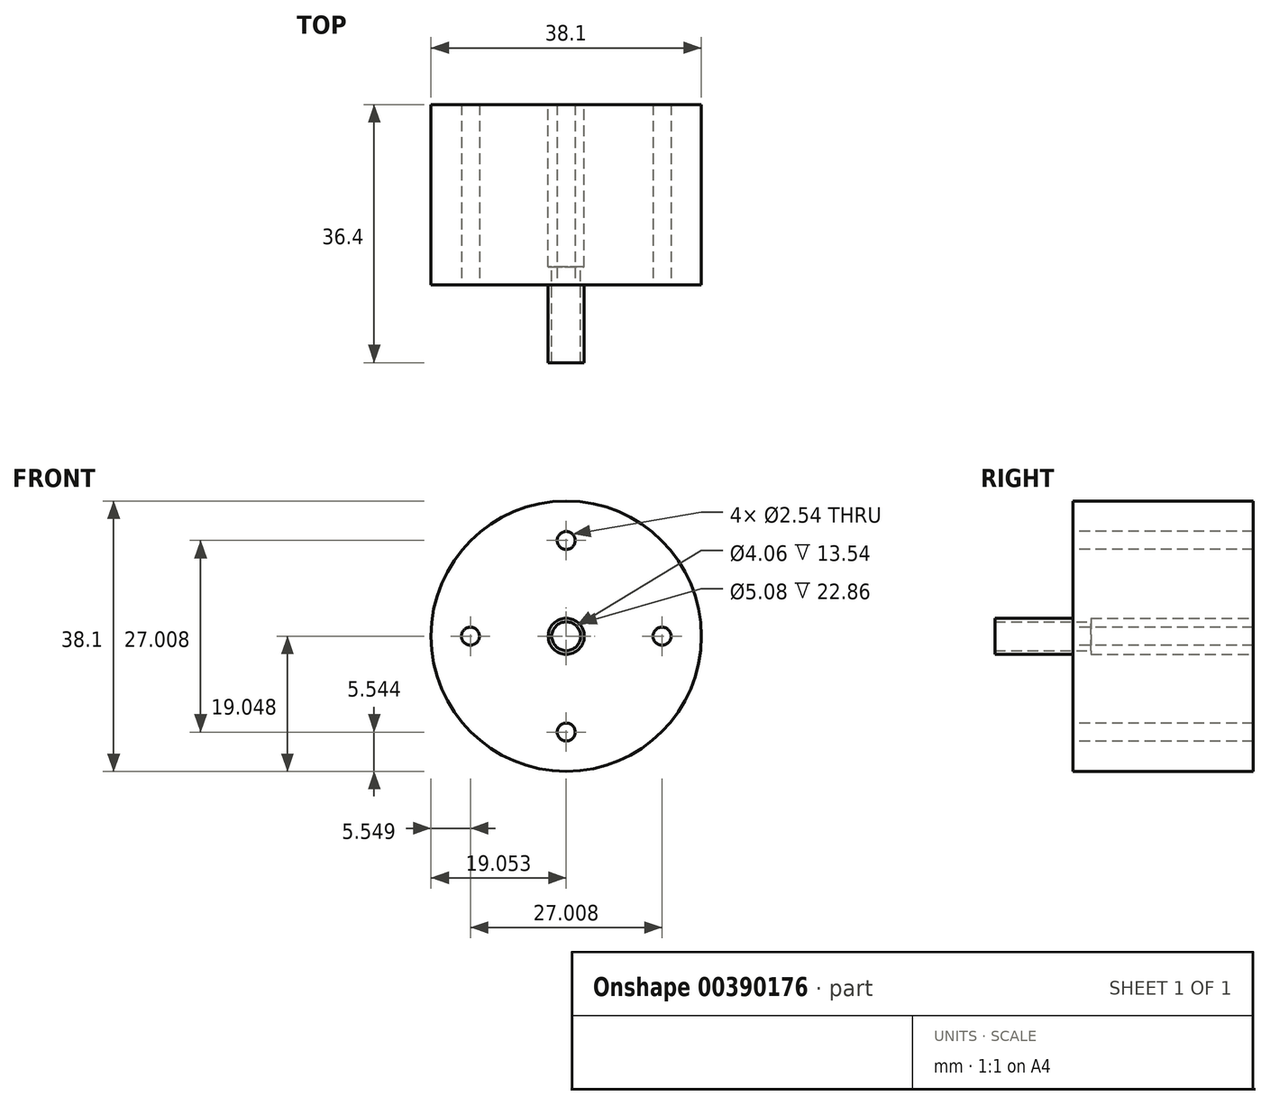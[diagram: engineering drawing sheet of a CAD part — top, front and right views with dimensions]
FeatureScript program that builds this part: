
annotation { "Feature Type Name" : "Feature", "Feature Type Description" : "" }
export const myFeature = defineFeature(function(context is Context, id is Id, definition is map)
    precondition{}
    {
        {
            var Q0;
            Q0=qCreatedBy(makeId("Front.planeOp"),FACE);
            var sketch = newSketch(context, id + "F0", { "sketchPlane" : qUnion([Q0])});
            skCircle(sketch, "E0", {"center": v(-6.44, 11.52) * mm, "radius": 19.05 * mm});
            skSolve(sketch);
        }
        {
            var Q0;
            Q0=qSketchRegion(id+"F0",true);
            extrude(context, id + "F1", {"entities" : qUnion([Q0]), "depth" : 25.4 * mm});
        }
        {
            var Q0;
            Q0=makeQuery(id+"F1.opExtrude","CAP_FACE",FACE,{"disambiguationData":[OSD([sQuery(id+"F0.wireOp",EDGE,"E0")])],"isStart":false});
            var sketch = newSketch(context, id + "F2", { "sketchPlane" : qUnion([Q0])});
            skCircle(sketch, "E1", {"center": v(-6.44, 11.52) * mm, "radius": 2.54 * mm});
            skCircle(sketch, "E2", {"center": v(-6.44, 11.52) * mm, "radius": 2.03 * mm});
            skSolve(sketch);
        }
        {
            var Q0;
            Q0=qSketchRegion(id+"F2",true);
            extrude(context, id + "F3", {"entities" : qUnion([Q0]), "operationType" : NewBodyOperationType.ADD, "depth" : 11 * mm});
        }
        {
            var Q0;
            Q0=makeQuery(id+"F3.boolean.opBoolean","SPLIT",FACE,{"disambiguationData":[TD([makeQuery(id+"F3.opExtrude","SWEPT_FACE",FACE,{"disambiguationData":[OSD([sQuery(id+"F2.wireOp",EDGE,"E2")])]})])],"derivedFrom":makeQuery(id+"F1.opExtrude","CAP_FACE",FACE,{"disambiguationData":[OSD([sQuery(id+"F0.wireOp",EDGE,"E0")])],"isStart":false})});
            extrude(context, id + "F4", {"entities" : qUnion([Q0]), "operationType" : NewBodyOperationType.REMOVE, "oppositeDirection" : true, "depth" : 25.4 * mm});
        }
        {
            var Q0;
            {var subQ0=sQuery(id+"F0.wireOp",EDGE,"E0");Q0=makeQuery(id+"F3.boolean.opBoolean","SPLIT",FACE,{"disambiguationData":[TD([makeQuery(id+"F1.opExtrude","SWEPT_FACE",FACE,{"disambiguationData":[OSD([subQ0])]})])],"derivedFrom":makeQuery(id+"F1.opExtrude","CAP_FACE",FACE,{"disambiguationData":[OSD([subQ0])],"isStart":false})});}
            var sketch = newSketch(context, id + "F5", { "sketchPlane" : qUnion([Q0])});
            skCircle(sketch, "E3", {"center": v(-19.94, 11.52) * mm, "radius": 1.27 * mm});
            skCircle(sketch, "E4.1.0", {"center": v(-6.44, -1.99) * mm, "radius": 1.27 * mm});
            skCircle(sketch, "E4.2.0", {"center": v(7.07, 11.52) * mm, "radius": 1.27 * mm});
            skCircle(sketch, "E4.3.0", {"center": v(-6.44, 25.02) * mm, "radius": 1.27 * mm});
            skPoint(sketch, "E4.center", {"position": v(-6.44, 11.52) * mm});
            skSolve(sketch);
        }
        {
            var Q0;
            Q0=qSketchRegion(id+"F5",true);
            extrude(context, id + "F6", {"entities" : qUnion([Q0]), "operationType" : NewBodyOperationType.REMOVE, "oppositeDirection" : true, "depth" : 25.4 * mm});
        }
        {
            var Q0;
            Q0=makeQuery(id+"F1.opExtrude","CAP_FACE",FACE,{"disambiguationData":[OSD([sQuery(id+"F0.wireOp",EDGE,"E0")])],"isStart":true});
            var sketch = newSketch(context, id + "F7", { "sketchPlane" : qUnion([Q0])});
            skCircle(sketch, "E5", {"center": v(6.44, 11.52) * mm, "radius": 2.54 * mm});
            skSolve(sketch);
        }
        {
            var Q0;
            Q0=makeQuery(id+"F7.imprint","IMPRINT",FACE,{"disambiguationData":[TD([[makeQuery(id+"F7.imprint","IMPRINT",EDGE,{"derivedFrom":sQuery(id+"F7.wireOp",EDGE,"E5")}),1.0]])]});
            extrude(context, id + "F8", {"entities" : qUnion([Q0]), "operationType" : NewBodyOperationType.REMOVE, "oppositeDirection" : true, "depth" : 22.86 * mm});
        }
    });
